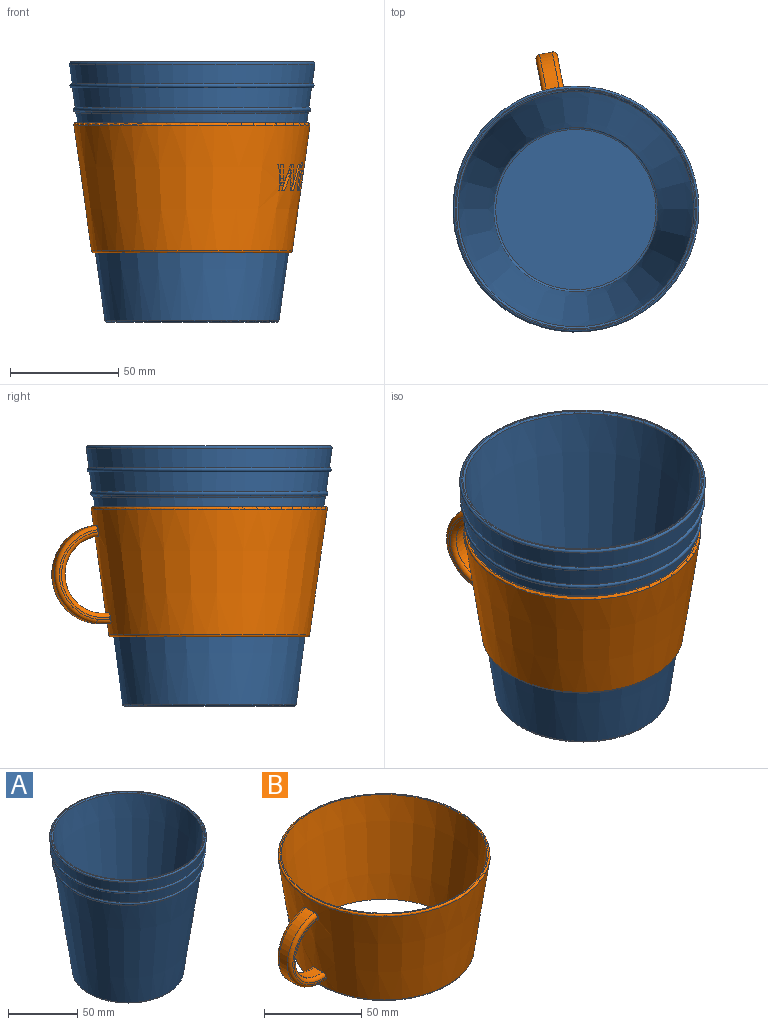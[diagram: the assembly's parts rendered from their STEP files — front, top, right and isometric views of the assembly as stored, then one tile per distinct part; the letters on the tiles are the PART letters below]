
ASSEMBLY  parts=2 mates=1
PART A: 14 faces, bbox 122.8x122.8x120 mm
  f0: plane 111.43x111.43mm, normal (0,0,1), area 176mm2, adj f9,f12
  f1: plane 78.26x78.26mm, normal (0,0,-1), area 4810.4mm2, adj f10
  f2: cone r=40mm half-angle=8deg, axis (0,0,1), area 28358.1mm2, adj f10,f11
  f3: torus R=53.78mm, axis (0,0,1), area 896.6mm2, adj f4,f11
  f4: cone r=53.91mm half-angle=8deg, axis (0,0,1), area 3118.3mm2, adj f3,f5
  f5: torus R=55.32mm, axis (0,0,1), area 1104.4mm2, adj f4,f6
  f6: cone r=55.46mm half-angle=8deg, axis (0,0,1), area 3153mm2, adj f5,f12
  f7: plane 73.92x73.92mm, normal (0,0,1), area 4291mm2, adj f13
  f8: cone r=52.98mm half-angle=8deg, axis (0,0,1), area 33853.3mm2, adj f9,f13
  f9: torus R=55.21mm, axis (0,0,1), area 491.1mm2, adj f0,f8
  f10: torus R=39.13mm, axis (0,0,1), area 357.3mm2, adj f1,f2
  f11: torus R=54.52mm, axis (0,0,1), area 353.8mm2, adj f2,f3
  f12: torus R=55.71mm, axis (0,0,1), area 605.9mm2, adj f0,f6
  f13: torus R=36.96mm, axis (0,0,1), area 337.7mm2, adj f7,f8
PART B: 192 faces, bbox 134.4x118.2x60.3 mm
  f0: cone r=54.64mm half-angle=8deg, axis (0,0,1), area 17900.9mm2, adj f4,f5,f6,f7,f8,f12,f13,f14
  f1: plane 106.98x106.98mm, normal (0,0,1), area 219.5mm2, adj f3,f4
  f2: plane 90.68x90.68mm, normal (0,0,-1), area 264.5mm2, adj f3,f5
  f3: cone r=52.83mm half-angle=8deg, axis (0,0,1), area 18507.8mm2, adj f1,f2
  f4: torus R=53.49mm, axis (0,0,1), area 582mm2, adj f0,f1
  f5: torus R=45.34mm, axis (0,0,-1), area 413.1mm2, adj f0,f2
  f6: cylinder r=2mm len=2.02mm, axis (0.14,0,-0.99), area 0.7mm2, adj f0,f10,f14,f15
  f7: cylinder r=2mm len=1.85mm, axis (-0.14,0,0.99), area 0.6mm2, adj f0,f11,f19,f23
  f8: plane 6.72x6mm, normal (0,0,-1), area 39.9mm2, adj f0,f9,f14,f20
  f9: cylinder r=22.87mm len=45.28mm, axis (0,1,0), area 392.3mm2, adj f8,f13,f16,f21
  f10: plane 41.28x23.75mm, normal (0,-1,0), area 63mm2, adj f6,f14,f15,f16,f17,f18
  f11: plane 41.28x23.75mm, normal (0,1,0), area 63mm2, adj f7,f19,f20,f21,f22,f23
  f12: cylinder r=17.87mm len=35.59mm, axis (0,1,0), area 339.6mm2, adj f0,f15,f19
  f13: plane 6x0.28mm, normal (0,0,1), area 1.3mm2, adj f0,f9,f18,f23
  f14: cylinder r=2mm len=6.72mm, axis (-1,0,0), area 20.7mm2, adj f0,f6,f8,f10,f16
  f15: torus R=19.87mm, axis (0,-1,0), area 185.6mm2, adj f0,f6,f10,f12,f17
  f16: torus R=20.87mm, axis (0,-1,0), area 198.4mm2, adj f9,f10,f14,f18
  f17: cylinder r=2mm len=1.85mm, axis (0.14,0,-0.99), area 0.6mm2, adj f0,f10,f15,f18
  f18: cylinder r=2mm len=2mm, axis (1,0,0), area 1.2mm2, adj f0,f10,f13,f16,f17
  f19: torus R=19.87mm, axis (0,-1,0), area 185.6mm2, adj f0,f7,f11,f12,f22
  f20: cylinder r=2mm len=6.72mm, axis (1,0,0), area 20.7mm2, adj f0,f8,f11,f21,f22
  f21: torus R=20.87mm, axis (0,-1,0), area 198.4mm2, adj f9,f11,f20,f23
  f22: cylinder r=2mm len=2.02mm, axis (-0.14,0,0.99), area 0.7mm2, adj f0,f11,f19,f20
  f23: cylinder r=2mm len=2mm, axis (-1,0,0), area 1.2mm2, adj f0,f7,f11,f13,f21
  f24: extruded ~2.15x1.18mm, area 1.9mm2, adj f0,f25,f49,f50
  f25: extruded ~2.29x2.17mm, area 3.9mm2, adj f0,f24,f26,f50
  f26: extruded ~4.52x2.95mm, area 4.6mm2, adj f0,f25,f27,f50
  f27: extruded ~3.04x1.72mm, area 2.4mm2, adj f0,f26,f28,f50
  f28: extruded ~2.56x1.33mm, area 1.9mm2, adj f0,f27,f29,f50
  f29: plane 2.08x1.69mm, normal (-1,0,0), area 2.7mm2, adj f0,f28,f30,f50
  f30: extruded ~2.8x1.58mm, area 2.2mm2, adj f0,f29,f31,f50
  f31: extruded ~2.89x1.55mm, area 2.2mm2, adj f0,f30,f32,f50
  f32: extruded ~2.69x1.37mm, area 2.6mm2, adj f0,f31,f33,f50
  f33: extruded ~1.76x0.49mm, area 0.8mm2, adj f0,f32,f34,f50
  f34: extruded ~2.18x0.63mm, area 1.1mm2, adj f0,f33,f35,f50
  f35: extruded ~2.67x1.19mm, area 1.8mm2, adj f0,f34,f36,f50
  f36: extruded ~2.92x1.57mm, area 2.4mm2, adj f0,f35,f37,f50
  f37: extruded ~2.09x0.87mm, area 1.5mm2, adj f0,f36,f38,f50
  f38: extruded ~1.71x1.21mm, area 1.6mm2, adj f0,f37,f39,f50
  f39: extruded ~1.91x1.75mm, area 2.9mm2, adj f0,f38,f40,f50
  f40: extruded ~3.69x2.71mm, area 3.9mm2, adj f0,f39,f41,f50
  f41: extruded ~5.1x3.25mm, area 5mm2, adj f0,f40,f42,f50
  f42: plane 2.04x1.82mm, normal (0.92,0,0.39), area 3mm2, adj f0,f41,f43,f50
  f43: extruded ~3.01x1.3mm, area 2.1mm2, adj f0,f42,f44,f50
  f44: extruded ~2.72x1.23mm, area 1.8mm2, adj f0,f43,f45,f50
  f45: extruded ~2.34x1.12mm, area 2mm2, adj f0,f44,f46,f50
  f46: extruded ~1.83x0.59mm, area 1mm2, adj f0,f45,f47,f50
  f47: extruded ~3.12x1.58mm, area 2.5mm2, adj f0,f46,f48,f50
  f48: extruded ~3.39x1.59mm, area 2.7mm2, adj f0,f47,f49,f50
  f49: extruded ~2.62x0.88mm, area 1.8mm2, adj f0,f24,f48,f50
  f50: cone r=53.49mm half-angle=8deg, axis (0,0,1), area 59.5mm2, adj f24,f25,f26,f27,f28,f29,f30,f31
  f51: extruded ~2.07x1.27mm, area 1.7mm2, adj f52,f70,f71,f189
  f52: extruded ~1.82x1.26mm, area 1.6mm2, adj f51,f53,f71,f189
  f53: extruded ~1.44x1.22mm, area 1.8mm2, adj f52,f54,f71,f189
  f54: plane 3.54x3.34mm, normal (0,0,-1), area 4.2mm2, adj f53,f70,f71,f189
  f55: extruded ~2.41x1.84mm, area 2.2mm2, adj f0,f56,f69,f71
  f56: extruded ~3.48x3.38mm, area 4.4mm2, adj f0,f55,f57,f71
  f57: extruded ~3.49x2.31mm, area 4.3mm2, adj f0,f56,f58,f71
  f58: extruded ~3.59x1.16mm, area 4.4mm2, adj f0,f57,f59,f71
  f59: extruded ~3.21x2.73mm, area 4.1mm2, adj f0,f58,f60,f71
  f60: extruded ~3.38x3.05mm, area 4mm2, adj f0,f59,f61,f71
  f61: extruded ~3.08x2.58mm, area 4.2mm2, adj f0,f60,f62,f71
  f62: plane 1.48x1.22mm, normal (1,0,0), area 1.6mm2, adj f0,f61,f63,f71
  f63: plane 5.96x5.1mm, normal (0,0,1), area 7.2mm2, adj f0,f62,f64,f71
  f64: extruded ~1.79x1.68mm, area 2.1mm2, adj f0,f63,f65,f71
  f65: extruded ~2.29x1.67mm, area 2.2mm2, adj f0,f64,f66,f71
  f66: extruded ~2.22x1.58mm, area 1.9mm2, adj f0,f65,f67,f71
  f67: extruded ~2.26x1.55mm, area 2.1mm2, adj f0,f66,f68,f71
  f68: plane 1.95x1.6mm, normal (1,0,0), area 2.5mm2, adj f0,f67,f69,f71
  f69: extruded ~2.18x1.41mm, area 1.9mm2, adj f0,f55,f68,f71
  f70: extruded ~1.77x1.44mm, area 1.9mm2, adj f51,f54,f71,f189
  f71: cone r=53.49mm half-angle=8deg, axis (0,0,1), area 57.3mm2, adj f51,f52,f53,f54,f55,f56,f57,f58
  f72: extruded ~1.6x1.27mm, area 1.5mm2, adj f73,f91,f92,f190
  f73: extruded ~1.39x1.26mm, area 1.5mm2, adj f72,f74,f92,f190
  f74: extruded ~1.44x1.11mm, area 1.6mm2, adj f73,f75,f92,f190
  f75: plane 3.54x2.27mm, normal (0,0,-1), area 3.8mm2, adj f74,f91,f92,f190
  f76: extruded ~1.84x1.75mm, area 2mm2, adj f0,f77,f90,f92
  f77: extruded ~3.48x2.33mm, area 4mm2, adj f0,f76,f78,f92
  f78: extruded ~3.49x1.87mm, area 4mm2, adj f0,f77,f79,f92
  f79: extruded ~3.59x1.27mm, area 4mm2, adj f0,f78,f80,f92
  f80: extruded ~3.21x1.83mm, area 3.8mm2, adj f0,f79,f81,f92
  f81: extruded ~3.05x2.38mm, area 3.6mm2, adj f0,f80,f82,f92
  f82: extruded ~3.08x2.03mm, area 3.7mm2, adj f0,f81,f83,f92
  f83: plane 1.29x1.22mm, normal (1,0,0), area 1.4mm2, adj f0,f82,f84,f92
  f84: plane 5.96x3.29mm, normal (0,0,1), area 6.4mm2, adj f0,f83,f85,f92
  f85: extruded ~1.68x1.5mm, area 1.9mm2, adj f0,f84,f86,f92
  f86: extruded ~1.72x1.67mm, area 1.9mm2, adj f0,f85,f87,f92
  f87: extruded ~1.64x1.58mm, area 1.7mm2, adj f0,f86,f88,f92
  f88: extruded ~1.65x1.55mm, area 1.8mm2, adj f0,f87,f89,f92
  f89: plane 1.95x1.4mm, normal (1,0,0), area 2.1mm2, adj f0,f88,f90,f92
  f90: extruded ~1.61x1.41mm, area 1.6mm2, adj f0,f76,f89,f92
  f91: extruded ~1.48x1.44mm, area 1.7mm2, adj f72,f75,f92,f190
  f92: cone r=53.49mm half-angle=8deg, axis (0,0,1), area 51.6mm2, adj f72,f73,f74,f75,f76,f77,f78,f79
  f93: plane 12.08x2.71mm, normal (-1,0,0), area 12.2mm2, adj f0,f94,f117,f118
  f94: plane 3.76x1.25mm, normal (0,0,-1), area 3.8mm2, adj f0,f93,f95,f118
  f95: extruded ~3.73x1.63mm, area 3.9mm2, adj f0,f94,f96,f118
  f96: extruded ~2.33x1.58mm, area 2.8mm2, adj f0,f95,f97,f118
  f97: extruded ~1.78x1.18mm, area 1.9mm2, adj f0,f96,f98,f118
  f98: extruded ~1.35x1.14mm, area 1.7mm2, adj f0,f97,f99,f118
  f99: plane 1.03x0.08mm, normal (1,0,0), area 0.1mm2, adj f0,f98,f100,f118
  f100: extruded ~1.66x1.46mm, area 2mm2, adj f0,f99,f101,f118
  f101: extruded ~1.87x1.4mm, area 2mm2, adj f0,f100,f102,f118
  f102: extruded ~2.58x1.2mm, area 3mm2, adj f0,f101,f103,f118
  f103: extruded ~3.24x1.38mm, area 3.5mm2, adj f0,f102,f117,f118
  f104: plane 1.59x1.16mm, normal (0,0,1), area 1.6mm2, adj f105,f115,f118,f120
  f105: plane 3.15x1.46mm, normal (1,0,0), area 3.2mm2, adj f104,f106,f118,f120
  f106: plane 1.67x1.17mm, normal (0,0,-1), area 1.7mm2, adj f105,f107,f118,f120
  f107: extruded ~1.56x1.16mm, area 1.7mm2, adj f106,f108,f118,f120
  f108: extruded ~1.24x1.12mm, area 1.4mm2, adj f107,f115,f118,f120
  f109: plane 2.69x1.39mm, normal (1,0,0), area 2.7mm2, adj f110,f116,f118,f119
  f110: plane 1.49x1.15mm, normal (0,0,-1), area 1.5mm2, adj f109,f111,f118,f119
  f111: extruded ~1.51x1.15mm, area 1.6mm2, adj f110,f112,f118,f119
  f112: extruded ~1.11x1.07mm, area 1.2mm2, adj f111,f113,f118,f119
  f113: extruded ~1.23x1mm, area 1.2mm2, adj f112,f114,f118,f119
  f114: extruded ~1.61x1.25mm, area 1.7mm2, adj f113,f116,f118,f119
  f115: extruded ~2.15x1.51mm, area 3mm2, adj f104,f108,f118,f120
  f116: plane 1.35x1.13mm, normal (0,0,1), area 1.4mm2, adj f109,f114,f118,f119
  f117: plane 4.52x1.34mm, normal (0,0,1), area 4.6mm2, adj f0,f93,f103,f118
  f118: cone r=53.49mm half-angle=8deg, axis (0,0,1), area 80.9mm2, adj f93,f94,f95,f96,f97,f98,f99,f100
  f119: cone r=54.64mm half-angle=8deg, axis (0,0,1), area 8.2mm2, adj f109,f110,f111,f112,f113,f114,f116
  f120: cone r=54.64mm half-angle=8deg, axis (0,0,1), area 9.6mm2, adj f104,f105,f106,f107,f108,f115
  f121: extruded ~1.27x1.05mm, area 1.4mm2, adj f122,f140,f141,f191
  f122: extruded ~1.26x1.23mm, area 1.4mm2, adj f121,f123,f141,f191
  f123: extruded ~1.44x1.29mm, area 1.6mm2, adj f122,f124,f141,f191
  f124: plane 3.54x1.37mm, normal (0,0,-1), area 3.6mm2, adj f123,f140,f141,f191
  f125: extruded ~1.84x1.18mm, area 1.9mm2, adj f0,f126,f139,f141
  f126: extruded ~3.48x1.3mm, area 3.9mm2, adj f0,f125,f127,f141
  f127: extruded ~3.49x1.3mm, area 3.9mm2, adj f0,f126,f128,f141
  f128: extruded ~3.59x1.75mm, area 4mm2, adj f0,f127,f129,f141
  f129: extruded ~3.21x1.62mm, area 3.6mm2, adj f0,f128,f130,f141
  f130: extruded ~3.05x1.11mm, area 3.4mm2, adj f0,f129,f131,f141
  f131: extruded ~3.08x1.41mm, area 3.4mm2, adj f0,f130,f132,f141
  f132: plane 1.22x1.18mm, normal (1,0,0), area 1.2mm2, adj f0,f131,f133,f141
  f133: plane 5.96x1.48mm, normal (0,0,1), area 6mm2, adj f0,f132,f134,f141
  f134: extruded ~1.68x1.17mm, area 1.9mm2, adj f0,f133,f135,f141
  f135: extruded ~1.67x1.11mm, area 1.9mm2, adj f0,f134,f136,f141
  f136: extruded ~1.58x1.16mm, area 1.6mm2, adj f0,f135,f137,f141
  f137: extruded ~1.55x1.16mm, area 1.7mm2, adj f0,f136,f138,f141
  f138: plane 1.95x1.28mm, normal (1,0,0), area 2mm2, adj f0,f137,f139,f141
  f139: extruded ~1.41x1.14mm, area 1.5mm2, adj f0,f125,f138,f141
  f140: extruded ~1.44x1.18mm, area 1.6mm2, adj f121,f124,f141,f191
  f141: cone r=53.49mm half-angle=8deg, axis (0,0,1), area 49.1mm2, adj f121,f122,f123,f124,f125,f126,f127,f128
  f142: plane 1.92x1.31mm, normal (1,0,0), area 2mm2, adj f0,f143,f151,f152
  f143: plane 7.29x3.27mm, normal (0,0,1), area 7.7mm2, adj f0,f142,f144,f152
  f144: plane 1.49x1.31mm, normal (-1,0,0), area 1.6mm2, adj f0,f143,f145,f152
  f145: plane 5.9x4.35mm, normal (-0.81,0,-0.59), area 7.7mm2, adj f0,f144,f146,f152
  f146: plane 4.02x2.38mm, normal (0,0,1), area 4.3mm2, adj f0,f145,f147,f152
  f147: plane 1.93x1.37mm, normal (-1,0,0), area 2.1mm2, adj f0,f146,f148,f152
  f148: plane 6.89x3.08mm, normal (0,0,-1), area 7.3mm2, adj f0,f147,f149,f152
  f149: plane 1.64x1.27mm, normal (1,0,0), area 1.7mm2, adj f0,f148,f150,f152
  f150: plane 5.74x4.22mm, normal (0.81,0,0.59), area 7.4mm2, adj f0,f149,f151,f152
  f151: plane 4.31x2.2mm, normal (0,0,-1), area 4.5mm2, adj f0,f142,f150,f152
  f152: cone r=53.49mm half-angle=8deg, axis (0,0,1), area 43.9mm2, adj f142,f143,f144,f145,f146,f147,f148,f149
  f153: plane 9.25x2.52mm, normal (1,0,0), area 10.1mm2, adj f0,f154,f156,f157
  f154: plane 2.52x2.29mm, normal (0,0,1), area 2.8mm2, adj f0,f153,f155,f157
  f155: plane 9.25x2.58mm, normal (-1,0,0), area 10.4mm2, adj f0,f154,f156,f157
  f156: plane 2.52x2.25mm, normal (0,0,-1), area 2.8mm2, adj f0,f153,f155,f157
  f157: cone r=53.49mm half-angle=8deg, axis (0,0,1), area 25.9mm2, adj f153,f154,f155,f156
  f158: extruded ~1.57x1.37mm, area 2.4mm2, adj f0,f159,f162,f163
  f159: extruded ~1.95x1.37mm, area 2.4mm2, adj f0,f158,f160,f163
  f160: extruded ~1.5x1.37mm, area 2.3mm2, adj f0,f159,f161,f163
  f161: extruded ~1.38x0.91mm, area 1.1mm2, adj f0,f160,f162,f163
  f162: extruded ~1.6x1.03mm, area 1.2mm2, adj f0,f158,f161,f163
  f163: cone r=53.49mm half-angle=8deg, axis (0,0,1), area 5.5mm2, adj f158,f159,f160,f161,f162
  f164: plane 12.35x5.16mm, normal (0.97,0,0.25), area 14.5mm2, adj f0,f165,f187,f188
  f165: plane 3.23x2.92mm, normal (0,0,1), area 3.6mm2, adj f0,f164,f166,f188
  f166: plane 6.35x1.64mm, normal (-0.97,0,0.25), area 8.3mm2, adj f0,f165,f167,f188
  f167: extruded ~1.4x1.29mm, area 1.8mm2, adj f0,f166,f168,f188
  f168: extruded ~1.43x1.35mm, area 1.9mm2, adj f0,f167,f169,f188
  f169: extruded ~1.76x1.43mm, area 1.9mm2, adj f0,f168,f170,f188
  f170: extruded ~1.82x1.41mm, area 1.9mm2, adj f0,f169,f171,f188
  f171: plane 6.45x4.09mm, normal (0.97,0,0.25), area 8.8mm2, adj f0,f170,f172,f188
  f172: plane 4.41x2.91mm, normal (0,0,1), area 4.2mm2, adj f0,f171,f173,f188
  f173: plane 12.18x3.19mm, normal (-0.97,0,0.25), area 19.4mm2, adj f0,f172,f174,f188
  f174: plane 4.43x2.52mm, normal (0,0,-1), area 3.9mm2, adj f0,f173,f175,f188
  f175: plane 6.61x1.74mm, normal (0.97,0,-0.23), area 9.9mm2, adj f0,f174,f176,f188
  f176: extruded ~3.16x1.48mm, area 4.6mm2, adj f0,f175,f177,f188
  f177: extruded ~1.93x1.46mm, area 2.1mm2, adj f0,f176,f178,f188
  f178: extruded ~2.02x1.53mm, area 2.2mm2, adj f0,f177,f179,f188
  f179: plane 6.9x4.34mm, normal (-0.97,0,-0.25), area 9.5mm2, adj f0,f178,f180,f188
  f180: plane 3.19x2.42mm, normal (0,0,-1), area 3.1mm2, adj f0,f179,f181,f188
  f181: plane 6.78x1.77mm, normal (0.97,0,-0.25), area 8.7mm2, adj f0,f180,f182,f188
  f182: extruded ~1.39x1.27mm, area 1.7mm2, adj f0,f181,f183,f188
  f183: extruded ~1.6x1.32mm, area 2mm2, adj f0,f182,f184,f188
  f184: extruded ~1.67x1.61mm, area 2mm2, adj f0,f183,f185,f188
  f185: extruded ~1.69x1.56mm, area 1.9mm2, adj f0,f184,f186,f188
  f186: plane 6.68x3.32mm, normal (-0.97,0,-0.23), area 8.1mm2, adj f0,f185,f187,f188
  f187: plane 2.55x2.52mm, normal (0,0,-1), area 2.9mm2, adj f0,f164,f186,f188
  f188: cone r=53.49mm half-angle=8deg, axis (0,0,1), area 134.1mm2, adj f164,f165,f166,f167,f168,f169,f170,f171
  f189: cone r=54.64mm half-angle=8deg, axis (0,0,1), area 5.9mm2, adj f51,f52,f53,f54,f70
  f190: cone r=54.64mm half-angle=8deg, axis (0,0,1), area 5.3mm2, adj f72,f73,f74,f75,f91
  f191: cone r=54.64mm half-angle=8deg, axis (0,0,1), area 5.1mm2, adj f121,f122,f123,f124,f140
PLACE A t=(-109.27,-47.73,23.05)mm fixed
PLACE B rot(axis=(0,0,-1),79.1deg) t=(-109.27,-47.73,23.73)mm
MATE cylindrical A.f2 <-> B.f0  axis (0,0,1) through (-109.27,-47.73,59.35)mm
